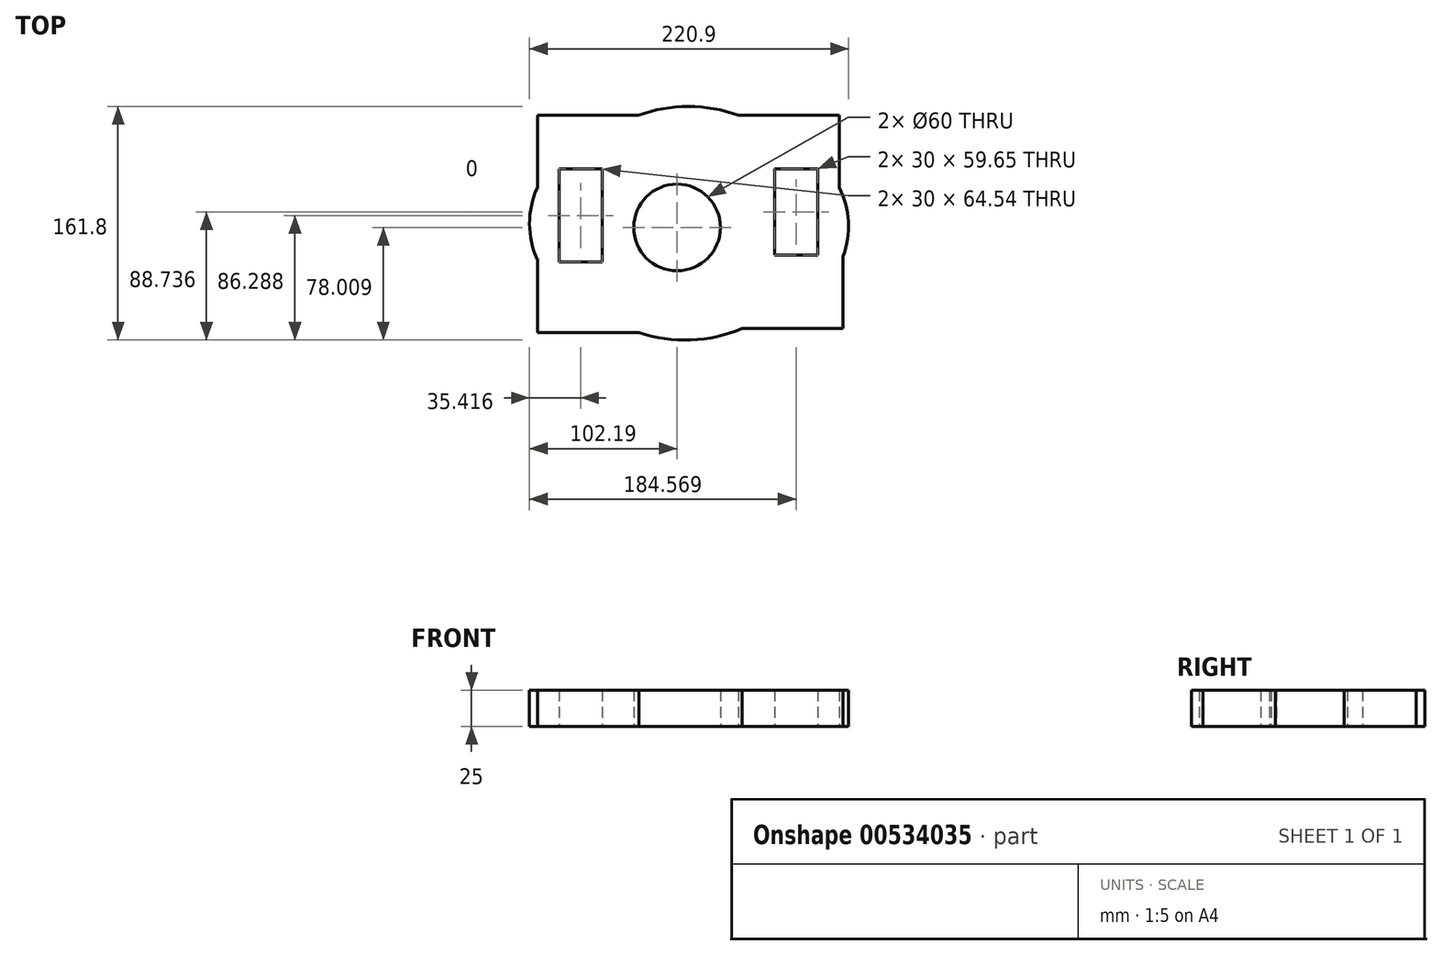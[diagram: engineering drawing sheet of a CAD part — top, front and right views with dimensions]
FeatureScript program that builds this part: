
annotation { "Feature Type Name" : "Feature", "Feature Type Description" : "" }
export const myFeature = defineFeature(function(context is Context, id is Id, definition is map)
    precondition{}
    {
        {
            var Q0;
            Q0=qCreatedBy(makeId("Top.planeOp"),FACE);
            var sketch = newSketch(context, id + "F0", { "sketchPlane" : qUnion([Q0])});
            skLineSegment(sketch, "E0", {"start": v(-69.78, 37.07) * mm, "end": v(0.22, 37.07) * mm});
            skLineSegment(sketch, "E1", {"start": v(-69.78, 37.07) * mm, "end": v(-69.78, -12.93) * mm});
            skArc(sketch, "E2", {"start": v(-69.78, -12.93) * mm, "mid": v(-75.2, -38.08) * mm, "end": v(-69.58, -63.2) * mm});
            skLineSegment(sketch, "E3", {"start": v(-69.58, -63.2) * mm, "end": v(-69.58, -113.2) * mm});
            skLineSegment(sketch, "E4", {"start": v(-69.58, -113.2) * mm, "end": v(0.42, -113.2) * mm});
            skArc(sketch, "E5", {"start": v(0.42, -113.2) * mm, "mid": v(36.44, -118.5) * mm, "end": v(71.98, -110.54) * mm});
            skLineSegment(sketch, "E6", {"start": v(71.98, -110.54) * mm, "end": v(141.98, -110.54) * mm});
            skLineSegment(sketch, "E7", {"start": v(141.98, -110.54) * mm, "end": v(141.98, -60.54) * mm});
            skArc(sketch, "E8", {"start": v(141.98, -60.54) * mm, "mid": v(145.6, -36.47) * mm, "end": v(139.37, -12.93) * mm});
            skLineSegment(sketch, "E9", {"start": v(139.37, -12.93) * mm, "end": v(139.37, 37.07) * mm});
            skLineSegment(sketch, "E10", {"start": v(139.37, 37.07) * mm, "end": v(69.37, 37.07) * mm});
            skArc(sketch, "E11", {"start": v(69.37, 37.07) * mm, "mid": v(34.8, 43.24) * mm, "end": v(0.22, 37.07) * mm});
            skCircle(sketch, "E12", {"center": v(26.99, -40.55) * mm, "radius": 30 * mm});
            skLineSegment(sketch, "E13", {"start": v(-54.78, 0) * mm, "end": v(-24.78, 0) * mm});
            skLineSegment(sketch, "E14", {"start": v(-24.78, 0) * mm, "end": v(-24.78, -64.54) * mm});
            skLineSegment(sketch, "E15", {"start": v(-24.78, -64.54) * mm, "end": v(-54.78, -64.54) * mm});
            skLineSegment(sketch, "E16", {"start": v(-54.78, -64.54) * mm, "end": v(-54.78, 0) * mm});
            skLineSegment(sketch, "E17", {"start": v(94.37, 0) * mm, "end": v(124.37, 0) * mm});
            skLineSegment(sketch, "E18", {"start": v(124.37, 0) * mm, "end": v(124.37, -59.65) * mm});
            skLineSegment(sketch, "E19", {"start": v(124.37, -59.65) * mm, "end": v(94.37, -59.65) * mm});
            skLineSegment(sketch, "E20", {"start": v(94.37, -59.65) * mm, "end": v(94.37, 0) * mm});
            skSolve(sketch);
        }
        {
            var Q0;
            Q0 = qSketchRegion(id + "F0", true);
            extrude(context, id + "F1", {"entities" : qUnion([Q0]), "depth" : 25 * mm, "offsetDistance" : 25 * mm});
        }
    });
